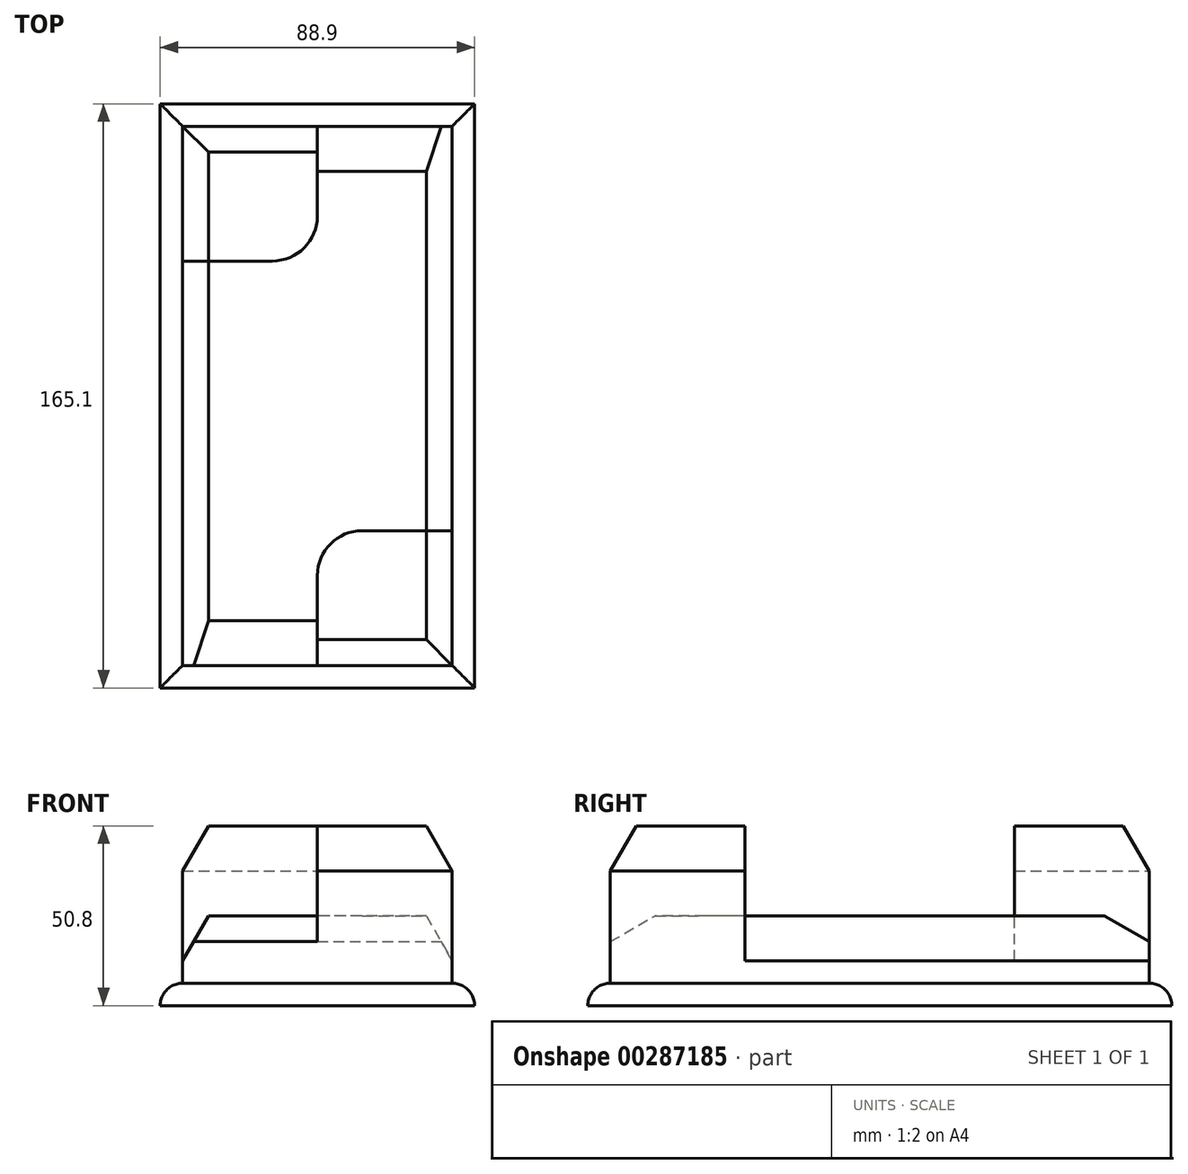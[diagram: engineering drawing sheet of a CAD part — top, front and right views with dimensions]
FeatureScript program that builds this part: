
annotation { "Feature Type Name" : "Feature", "Feature Type Description" : "" }
export const myFeature = defineFeature(function(context is Context, id is Id, definition is map)
    precondition{}
    {
        {
            var Q0;
            Q0=qCreatedBy(makeId("Top.planeOp"),FACE);
            var sketch = newSketch(context, id + "F0", { "sketchPlane" : qUnion([Q0])});
            skLineSegment(sketch, "E0.bottom", {"start": v(38.1, 76.2) * mm, "end": v(-38.1, 76.2) * mm});
            skLineSegment(sketch, "E0.top", {"start": v(38.1, -76.2) * mm, "end": v(-38.1, -76.2) * mm});
            skLineSegment(sketch, "E0.left", {"start": v(38.1, 76.2) * mm, "end": v(38.1, -76.2) * mm});
            skLineSegment(sketch, "E0.right", {"start": v(-38.1, 76.2) * mm, "end": v(-38.1, -76.2) * mm});
            skPoint(sketch, "E0.middle", {"position": v(0, 0) * mm});
            skLineSegment(sketch, "E1.0", {"start": v(44.45, 82.55) * mm, "end": v(-44.45, 82.55) * mm});
            skLineSegment(sketch, "E1.1", {"start": v(44.45, 82.55) * mm, "end": v(44.45, -82.55) * mm});
            skLineSegment(sketch, "E1.2", {"start": v(44.45, -82.55) * mm, "end": v(-44.45, -82.55) * mm});
            skLineSegment(sketch, "E1.3", {"start": v(-44.45, 82.55) * mm, "end": v(-44.45, -82.55) * mm});
            skLineSegment(sketch, "E2", {"start": v(0, -76.2) * mm, "end": v(0, -50.8) * mm});
            skPoint(sketch, "E2.endSnap0", {"position": v(0, -76.2) * mm});
            skLineSegment(sketch, "E3", {"start": v(12.7, -38.1) * mm, "end": v(38.1, -38.1) * mm});
            skLineSegment(sketch, "E4", {"start": v(0, 76.2) * mm, "end": v(0, 50.8) * mm});
            skPoint(sketch, "E4.endSnap0", {"position": v(0, 76.2) * mm});
            skLineSegment(sketch, "E5", {"start": v(-12.7, 38.1) * mm, "end": v(-38.1, 38.1) * mm});
            skPoint(sketch, "E6.visualSharp", {"position": v(0, 38.1) * mm});
            skArc(sketch, "E6.filletArc", {"start": v(-12.7, 38.1) * mm, "mid": v(-3.72, 41.82) * mm, "end": v(0, 50.8) * mm});
            skPoint(sketch, "E7.visualSharp", {"position": v(0, -38.1) * mm});
            skArc(sketch, "E7.filletArc", {"start": v(12.7, -38.1) * mm, "mid": v(3.72, -41.82) * mm, "end": v(0, -50.8) * mm});
            skSolve(sketch);
        }
        {
            var Q0;
            Q0 = qSketchRegion(id + "F0", true);
            extrude(context, id + "F1", {"entities" : qUnion([Q0]), "depth" : 6.35 * mm});
        }
        {
            var Q0;
            {var subQ8=sQuery(id+"F0.wireOp",EDGE,"E2");Q0=makeQuery(id+"F0.imprint","IMPRINT",FACE,{"disambiguationData":[TD([[makeQuery(id+"F0.imprint","IMPRINT",EDGE,{"derivedFrom":subQ8}),1.0]])]});}
            extrude(context, id + "F2", {"entities" : qUnion([Q0]), "operationType" : NewBodyOperationType.ADD, "depth" : 25.4 * mm});
        }
        {
            var Q0;
            {var subQ1=sQuery(id+"F0.wireOp",EDGE,"E4");Q0=makeQuery(id+"F0.imprint","IMPRINT",FACE,{"disambiguationData":[TD([[makeQuery(id+"F0.imprint","IMPRINT",EDGE,{"derivedFrom":subQ1}),-1.0]])]});}
            var Q1;
            {var subQ4=sQuery(id+"F0.wireOp",EDGE,"E2");Q1=makeQuery(id+"F0.imprint","IMPRINT",FACE,{"disambiguationData":[TD([[makeQuery(id+"F0.imprint","IMPRINT",EDGE,{"derivedFrom":subQ4}),-1.0]])]});}
            extrude(context, id + "F3", {"entities" : qUnion([Q0, Q1]), "operationType" : NewBodyOperationType.ADD, "depth" : 50.8 * mm});
        }
        {
            var Q0;
            Q0=makeQuery(id+"F3.opExtrude","CAP_EDGE",EDGE,{"disambiguationData":[OSD([sQuery(id+"F0.wireOp",EDGE,"E0.right")])],"isStart":false});
            var Q1;
            Q1=makeQuery(id+"F3.opExtrude","CAP_EDGE",EDGE,{"disambiguationData":[OSD([sQuery(id+"F0.wireOp",EDGE,"E0.bottom")])],"isStart":false});
            var Q2;
            Q2=makeQuery(id+"F2.opExtrude","CAP_EDGE",EDGE,{"disambiguationData":[OSD([sQuery(id+"F0.wireOp",EDGE,"E0.right")])],"isStart":false});
            var Q3;
            Q3=makeQuery(id+"F2.opExtrude","CAP_EDGE",EDGE,{"disambiguationData":[OSD([sQuery(id+"F0.wireOp",EDGE,"E0.top")])],"isStart":false});
            chamfer(context, id + "F4", {"entities" : qUnion([Q0, Q1, Q2, Q3]), "chamferType" : ChamferType.OFFSET_ANGLE, "width" : 12.7 * mm, "oppositeDirection" : true, "angle" : 30 * degree, "tangentPropagation" : true});
        }
        {
            var Q0;
            Q0=makeQuery(id+"F3.opExtrude","CAP_EDGE",EDGE,{"disambiguationData":[OSD([sQuery(id+"F0.wireOp",EDGE,"E0.left")])],"isStart":false});
            var Q1;
            Q1=makeQuery(id+"F3.opExtrude","CAP_EDGE",EDGE,{"disambiguationData":[OSD([sQuery(id+"F0.wireOp",EDGE,"E0.top")])],"isStart":false});
            var Q2;
            Q2=makeQuery(id+"F2.opExtrude","CAP_EDGE",EDGE,{"disambiguationData":[OSD([sQuery(id+"F0.wireOp",EDGE,"E0.left")])],"isStart":false});
            var Q3;
            Q3=makeQuery(id+"F2.opExtrude","CAP_EDGE",EDGE,{"disambiguationData":[OSD([sQuery(id+"F0.wireOp",EDGE,"E0.bottom")])],"isStart":false});
            chamfer(context, id + "F5", {"entities" : qUnion([Q0, Q1, Q2, Q3]), "chamferType" : ChamferType.OFFSET_ANGLE, "width" : 12.7 * mm, "oppositeDirection" : false, "angle" : 30 * degree, "tangentPropagation" : true});
        }
        {
            var Q0;
            Q0=makeQuery(id+"F1.opExtrude","CAP_EDGE",EDGE,{"disambiguationData":[OSD([sQuery(id+"F0.wireOp",EDGE,"E1.3")])],"isStart":false});
            var Q1;
            Q1=makeQuery(id+"F1.opExtrude","CAP_EDGE",EDGE,{"disambiguationData":[OSD([sQuery(id+"F0.wireOp",EDGE,"E1.2")])],"isStart":false});
            var Q2;
            Q2=makeQuery(id+"F1.opExtrude","CAP_EDGE",EDGE,{"disambiguationData":[OSD([sQuery(id+"F0.wireOp",EDGE,"E1.0")])],"isStart":false});
            var Q3;
            Q3=makeQuery(id+"F1.opExtrude","CAP_EDGE",EDGE,{"disambiguationData":[OSD([sQuery(id+"F0.wireOp",EDGE,"E1.1")])],"isStart":false});
            fillet(context, id + "F6", {"entities" : qUnion([Q0, Q1, Q2, Q3]), "radius" : 6.35 * mm, "tangentPropagation" : true, "allowEdgeOverflow" : false});
        }
    });
